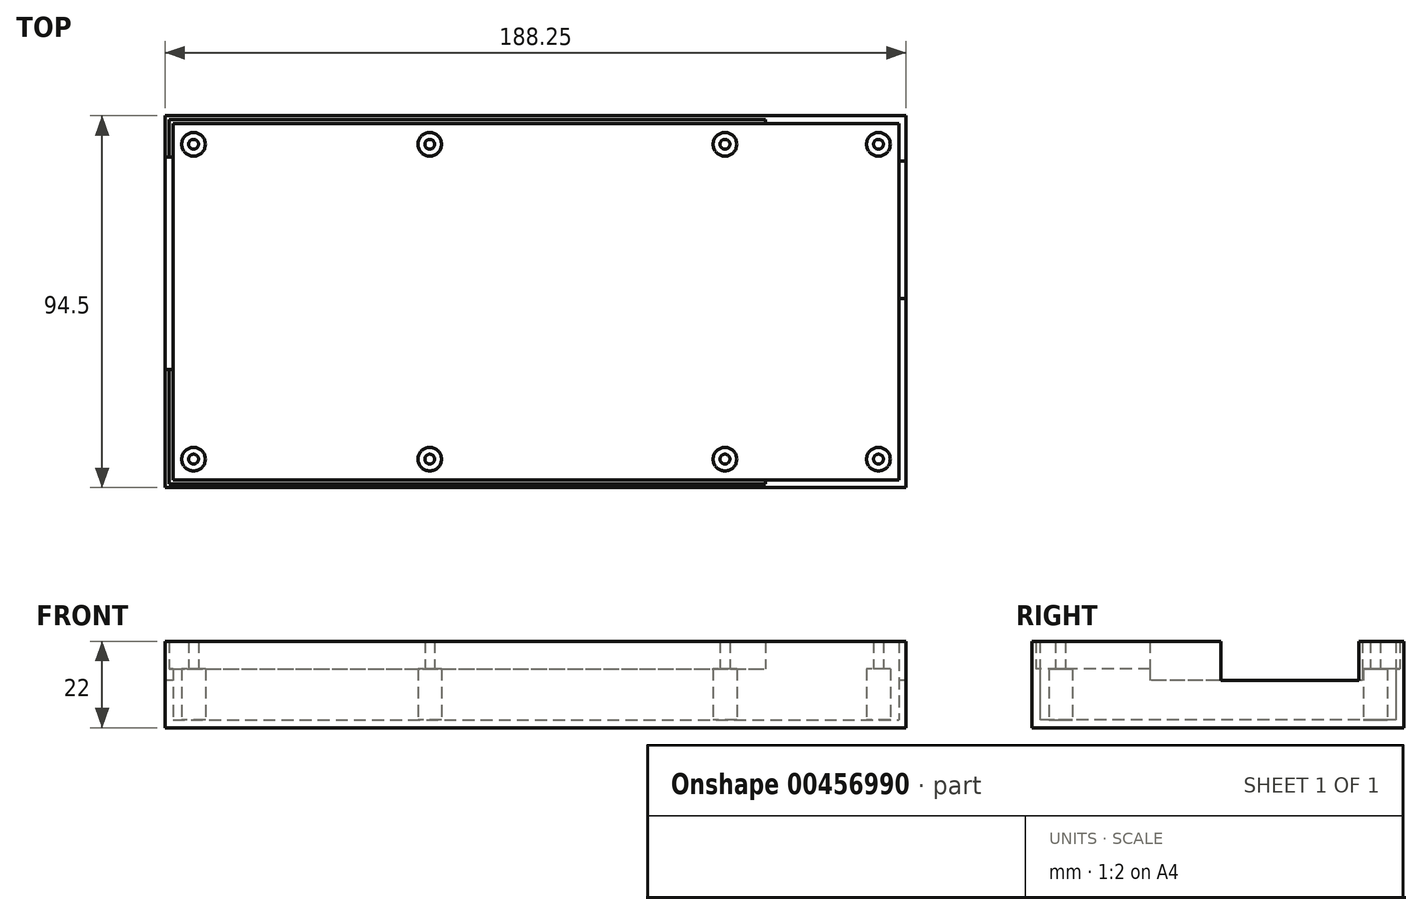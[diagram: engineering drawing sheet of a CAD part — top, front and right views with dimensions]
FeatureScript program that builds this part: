
annotation { "Feature Type Name" : "Feature", "Feature Type Description" : "" }
export const myFeature = defineFeature(function(context is Context, id is Id, definition is map)
    precondition{}
    {
        {
            var Q0;
            Q0=qCreatedBy(makeId("Top.planeOp"),FACE);
            var sketch = newSketch(context, id + "F0", { "sketchPlane" : qUnion([Q0])});
            skLineSegment(sketch, "E0.bottom", {"start": v(-142.25, 0) * mm, "end": v(46, 0) * mm});
            skLineSegment(sketch, "E0.top", {"start": v(-142.25, -94.5) * mm, "end": v(46, -94.5) * mm});
            skLineSegment(sketch, "E0.left", {"start": v(-142.25, 0) * mm, "end": v(-142.25, -94.5) * mm});
            skLineSegment(sketch, "E0.right", {"start": v(46, 0) * mm, "end": v(46, -94.5) * mm});
            skLineSegment(sketch, "E1.bottom", {"start": v(-140.25, -2) * mm, "end": v(44.25, -2) * mm});
            skLineSegment(sketch, "E1.top", {"start": v(-140.25, -92.5) * mm, "end": v(44.25, -92.5) * mm});
            skLineSegment(sketch, "E1.left", {"start": v(-140.25, -2) * mm, "end": v(-140.25, -92.5) * mm});
            skLineSegment(sketch, "E1.right", {"start": v(44.25, -2) * mm, "end": v(44.25, -92.5) * mm});
            skCircle(sketch, "E2", {"center": v(-135, -87.25) * mm, "radius": 3 * mm});
            skCircle(sketch, "E3", {"center": v(-135, -7.25) * mm, "radius": 3 * mm});
            skCircle(sketch, "E4", {"center": v(-75, -87.25) * mm, "radius": 3 * mm});
            skCircle(sketch, "E5", {"center": v(-75, -7.25) * mm, "radius": 3 * mm});
            skCircle(sketch, "E6", {"center": v(0, -7.25) * mm, "radius": 3 * mm});
            skCircle(sketch, "E7", {"center": v(0, -87.25) * mm, "radius": 3 * mm});
            skCircle(sketch, "E8", {"center": v(39, -87.25) * mm, "radius": 3 * mm});
            skCircle(sketch, "E9", {"center": v(39, -7.25) * mm, "radius": 3 * mm});
            skCircle(sketch, "E10", {"center": v(-135, -87.25) * mm, "radius": 1.25 * mm});
            skCircle(sketch, "E11", {"center": v(-75, -87.25) * mm, "radius": 1.25 * mm});
            skCircle(sketch, "E12", {"center": v(0, -87.25) * mm, "radius": 1.25 * mm});
            skCircle(sketch, "E13", {"center": v(39, -87.25) * mm, "radius": 1.25 * mm});
            skCircle(sketch, "E14", {"center": v(-135, -7.25) * mm, "radius": 1.25 * mm});
            skCircle(sketch, "E15", {"center": v(-75, -7.25) * mm, "radius": 1.25 * mm});
            skCircle(sketch, "E16", {"center": v(0, -7.25) * mm, "radius": 1.25 * mm});
            skCircle(sketch, "E17", {"center": v(39, -7.25) * mm, "radius": 1.25 * mm});
            skLineSegment(sketch, "E18", {"start": v(10.25, -2) * mm, "end": v(10.25, 0) * mm});
            skLineSegment(sketch, "E19", {"start": v(10.25, -92.5) * mm, "end": v(10.25, -94.5) * mm});
            skLineSegment(sketch, "E20", {"start": v(10.25, -93.5) * mm, "end": v(-141.25, -93.5) * mm});
            skLineSegment(sketch, "E21", {"start": v(-141.25, -1) * mm, "end": v(-141.25, -93.5) * mm});
            skLineSegment(sketch, "E22", {"start": v(-141.25, -1) * mm, "end": v(10.25, -1) * mm});
            skLineSegment(sketch, "E23", {"start": v(-140.25, -64.5) * mm, "end": v(-141.25, -64.5) * mm});
            skLineSegment(sketch, "E24", {"start": v(-140.25, -10.5) * mm, "end": v(-141.25, -10.5) * mm});
            skLineSegment(sketch, "E25", {"start": v(44.25, -46.5) * mm, "end": v(46, -46.5) * mm});
            skLineSegment(sketch, "E26", {"start": v(46, -11.5) * mm, "end": v(44.25, -11.5) * mm});
            skLineSegment(sketch, "E27", {"start": v(-141.25, -10.5) * mm, "end": v(-142.25, -10.5) * mm});
            skLineSegment(sketch, "E28", {"start": v(-141.25, -64.5) * mm, "end": v(-142.25, -64.5) * mm});
            skSolve(sketch);
        }
        {
            var Q0;
            Q0=makeQuery(id+"F0.imprint","IMPRINT",FACE,{"disambiguationData":[TD([[makeQuery(id+"F0.imprint","IMPRINT",EDGE,{"derivedFrom":sQuery(id+"F0.wireOp",EDGE,"E2")}),-1.0]])]});
            var Q1;
            {var subQ0=sQuery(id+"F0.wireOp",EDGE,"E22");Q1=makeQuery(id+"F0.imprint","IMPRINT",FACE,{"disambiguationData":[TD([[makeQuery(id+"F0.imprint","IMPRINT",EDGE,{"derivedFrom":subQ0}),1.0]])]});}
            var Q2;
            Q2=makeQuery(id+"F0.imprint","IMPRINT",FACE,{"disambiguationData":[TD([[makeQuery(id+"F0.imprint","IMPRINT",EDGE,{"derivedFrom":sQuery(id+"F0.wireOp",EDGE,"E14")}),1.0]])]});
            var Q3;
            Q3=makeQuery(id+"F0.imprint","IMPRINT",FACE,{"disambiguationData":[TD([[makeQuery(id+"F0.imprint","IMPRINT",EDGE,{"derivedFrom":sQuery(id+"F0.wireOp",EDGE,"E3")}),1.0]])]});
            var Q4;
            Q4=makeQuery(id+"F0.imprint","IMPRINT",FACE,{"disambiguationData":[TD([[makeQuery(id+"F0.imprint","IMPRINT",EDGE,{"derivedFrom":sQuery(id+"F0.wireOp",EDGE,"E5")}),1.0]])]});
            var Q5;
            Q5=makeQuery(id+"F0.imprint","IMPRINT",FACE,{"disambiguationData":[TD([[makeQuery(id+"F0.imprint","IMPRINT",EDGE,{"derivedFrom":sQuery(id+"F0.wireOp",EDGE,"E16")}),1.0]])]});
            var Q6;
            Q6=makeQuery(id+"F0.imprint","IMPRINT",FACE,{"disambiguationData":[TD([[makeQuery(id+"F0.imprint","IMPRINT",EDGE,{"derivedFrom":sQuery(id+"F0.wireOp",EDGE,"E17")}),1.0]])]});
            var Q7;
            Q7=makeQuery(id+"F0.imprint","IMPRINT",FACE,{"disambiguationData":[TD([[makeQuery(id+"F0.imprint","IMPRINT",EDGE,{"derivedFrom":sQuery(id+"F0.wireOp",EDGE,"E9")}),1.0]])]});
            var Q8;
            Q8=makeQuery(id+"F0.imprint","IMPRINT",FACE,{"disambiguationData":[TD([[makeQuery(id+"F0.imprint","IMPRINT",EDGE,{"derivedFrom":sQuery(id+"F0.wireOp",EDGE,"E7")}),1.0]])]});
            var Q9;
            Q9=makeQuery(id+"F0.imprint","IMPRINT",FACE,{"disambiguationData":[TD([[makeQuery(id+"F0.imprint","IMPRINT",EDGE,{"derivedFrom":sQuery(id+"F0.wireOp",EDGE,"E6")}),1.0]])]});
            var Q10;
            Q10=makeQuery(id+"F0.imprint","IMPRINT",FACE,{"disambiguationData":[TD([[makeQuery(id+"F0.imprint","IMPRINT",EDGE,{"derivedFrom":sQuery(id+"F0.wireOp",EDGE,"E8")}),1.0]])]});
            var Q11;
            Q11=makeQuery(id+"F0.imprint","IMPRINT",FACE,{"disambiguationData":[TD([[makeQuery(id+"F0.imprint","IMPRINT",EDGE,{"derivedFrom":sQuery(id+"F0.wireOp",EDGE,"E13")}),1.0]])]});
            var Q12;
            Q12=makeQuery(id+"F0.imprint","IMPRINT",FACE,{"disambiguationData":[TD([[makeQuery(id+"F0.imprint","IMPRINT",EDGE,{"derivedFrom":sQuery(id+"F0.wireOp",EDGE,"E12")}),1.0]])]});
            var Q13;
            Q13=makeQuery(id+"F0.imprint","IMPRINT",FACE,{"disambiguationData":[TD([[makeQuery(id+"F0.imprint","IMPRINT",EDGE,{"derivedFrom":sQuery(id+"F0.wireOp",EDGE,"E15")}),1.0]])]});
            var Q14;
            Q14=makeQuery(id+"F0.imprint","IMPRINT",FACE,{"disambiguationData":[TD([[makeQuery(id+"F0.imprint","IMPRINT",EDGE,{"derivedFrom":sQuery(id+"F0.wireOp",EDGE,"E2")}),1.0]])]});
            var Q15;
            Q15=makeQuery(id+"F0.imprint","IMPRINT",FACE,{"disambiguationData":[TD([[makeQuery(id+"F0.imprint","IMPRINT",EDGE,{"derivedFrom":sQuery(id+"F0.wireOp",EDGE,"E10")}),1.0]])]});
            var Q16;
            Q16=makeQuery(id+"F0.imprint","IMPRINT",FACE,{"disambiguationData":[TD([[makeQuery(id+"F0.imprint","IMPRINT",EDGE,{"derivedFrom":sQuery(id+"F0.wireOp",EDGE,"E11")}),1.0]])]});
            var Q17;
            Q17=makeQuery(id+"F0.imprint","IMPRINT",FACE,{"disambiguationData":[TD([[makeQuery(id+"F0.imprint","IMPRINT",EDGE,{"derivedFrom":sQuery(id+"F0.wireOp",EDGE,"E4")}),1.0]])]});
            var Q18;
            {var subQ0=sQuery(id+"F0.wireOp",EDGE,"E25");Q18=makeQuery(id+"F0.imprint","IMPRINT",FACE,{"disambiguationData":[TD([[makeQuery(id+"F0.imprint","IMPRINT",EDGE,{"derivedFrom":subQ0}),1.0]])]});}
            var Q19;
            {var subQ0=sQuery(id+"F0.wireOp",EDGE,"E23");var subQ1=sQuery(id+"F0.wireOp",EDGE,"E1.left");var subQ2=makeQuery(id+"F0.imprint","INTERSECT",VERTEX,{"derivedFrom":[subQ1,subQ0]});Q19=makeQuery(id+"F0.imprint","IMPRINT",FACE,{"disambiguationData":[TD([[makeQuery(id+"F0.imprint","IMPRINT",EDGE,{"disambiguationData":[TD([[subQ2,1.0]])],"derivedFrom":subQ1}),-1.0]])]});}
            var Q20;
            {var subQ0=sQuery(id+"F0.wireOp",EDGE,"E22");Q20=makeQuery(id+"F0.imprint","IMPRINT",FACE,{"disambiguationData":[TD([[makeQuery(id+"F0.imprint","IMPRINT",EDGE,{"derivedFrom":subQ0}),-1.0]])]});}
            var Q21;
            {var subQ3=sQuery(id+"F0.wireOp",EDGE,"E26");Q21=makeQuery(id+"F0.imprint","IMPRINT",FACE,{"disambiguationData":[TD([[makeQuery(id+"F0.imprint","IMPRINT",EDGE,{"derivedFrom":subQ3}),-1.0]])]});}
            var Q22;
            {var subQ0=sQuery(id+"F0.wireOp",EDGE,"E20");Q22=makeQuery(id+"F0.imprint","IMPRINT",FACE,{"disambiguationData":[TD([[makeQuery(id+"F0.imprint","IMPRINT",EDGE,{"derivedFrom":subQ0}),-1.0]])]});}
            var Q23;
            {var subQ3=sQuery(id+"F0.wireOp",EDGE,"E25");Q23=makeQuery(id+"F0.imprint","IMPRINT",FACE,{"disambiguationData":[TD([[makeQuery(id+"F0.imprint","IMPRINT",EDGE,{"derivedFrom":subQ3}),-1.0]])]});}
            var Q24;
            {var subQ0=sQuery(id+"F0.wireOp",EDGE,"E20");Q24=makeQuery(id+"F0.imprint","IMPRINT",FACE,{"disambiguationData":[TD([[makeQuery(id+"F0.imprint","IMPRINT",EDGE,{"derivedFrom":subQ0}),1.0]])]});}
            var Q25;
            {var subQ0=sQuery(id+"F0.wireOp",EDGE,"E23");var subQ1=sQuery(id+"F0.wireOp",EDGE,"E0.left");var subQ2=makeQuery(id+"F0.imprint","INTERSECT",VERTEX,{"derivedFrom":[subQ1,subQ0]});Q25=makeQuery(id+"F0.imprint","IMPRINT",FACE,{"disambiguationData":[TD([[makeQuery(id+"F0.imprint","IMPRINT",EDGE,{"disambiguationData":[TD([[subQ2,1.0]])],"derivedFrom":subQ1}),1.0]])]});}
            extrude(context, id + "F1", {"entities" : qUnion([Q0, Q1, Q2, Q3, Q4, Q5, Q6, Q7, Q8, Q9, Q10, Q11, Q12, Q13, Q14, Q15, Q16, Q17, Q18, Q19, Q20, Q21, Q22, Q23, Q24, Q25]), "oppositeDirection" : true, "depth" : 2 * mm, "offsetDistance" : 25 * mm});
        }
        {
            var Q0;
            Q0=makeQuery(id+"F0.imprint","IMPRINT",FACE,{"disambiguationData":[TD([[makeQuery(id+"F0.imprint","IMPRINT",EDGE,{"derivedFrom":sQuery(id+"F0.wireOp",EDGE,"E0.bottom")}),-1.0]])]});
            var Q1;
            {var subQ3=sQuery(id+"F0.wireOp",EDGE,"E26");Q1=makeQuery(id+"F0.imprint","IMPRINT",FACE,{"disambiguationData":[TD([[makeQuery(id+"F0.imprint","IMPRINT",EDGE,{"derivedFrom":subQ3}),-1.0]])]});}
            var Q2;
            {var subQ3=sQuery(id+"F0.wireOp",EDGE,"E25");Q2=makeQuery(id+"F0.imprint","IMPRINT",FACE,{"disambiguationData":[TD([[makeQuery(id+"F0.imprint","IMPRINT",EDGE,{"derivedFrom":subQ3}),-1.0]])]});}
            var Q3;
            {var subQ0=sQuery(id+"F0.wireOp",EDGE,"E20");Q3=makeQuery(id+"F0.imprint","IMPRINT",FACE,{"disambiguationData":[TD([[makeQuery(id+"F0.imprint","IMPRINT",EDGE,{"derivedFrom":subQ0}),1.0]])]});}
            extrude(context, id + "F2", {"entities" : qUnion([Q0, Q1, Q2, Q3]), "operationType" : NewBodyOperationType.ADD, "depth" : 20 * mm, "offsetDistance" : 25 * mm});
        }
        {
            var Q0;
            {var subQ0=sQuery(id+"F0.wireOp",EDGE,"E22");Q0=makeQuery(id+"F0.imprint","IMPRINT",FACE,{"disambiguationData":[TD([[makeQuery(id+"F0.imprint","IMPRINT",EDGE,{"derivedFrom":subQ0}),-1.0]])]});}
            var Q1;
            {var subQ0=sQuery(id+"F0.wireOp",EDGE,"E20");Q1=makeQuery(id+"F0.imprint","IMPRINT",FACE,{"disambiguationData":[TD([[makeQuery(id+"F0.imprint","IMPRINT",EDGE,{"derivedFrom":subQ0}),-1.0]])]});}
            extrude(context, id + "F3", {"entities" : qUnion([Q0, Q1]), "operationType" : NewBodyOperationType.ADD, "depth" : 13 * mm, "offsetDistance" : 25 * mm});
        }
        {
            var Q0;
            {var subQ0=sQuery(id+"F0.wireOp",EDGE,"E23");Q0=makeQuery(id+"F0.imprint","IMPRINT",FACE,{"disambiguationData":[TD([[makeQuery(id+"F0.imprint","IMPRINT",EDGE,{"derivedFrom":subQ0}),-1.0]])]});}
            var Q1;
            {var subQ0=sQuery(id+"F0.wireOp",EDGE,"E27");Q1=makeQuery(id+"F0.imprint","IMPRINT",FACE,{"disambiguationData":[TD([[makeQuery(id+"F0.imprint","IMPRINT",EDGE,{"derivedFrom":subQ0}),1.0]])]});}
            var Q2;
            {var subQ0=sQuery(id+"F0.wireOp",EDGE,"E25");Q2=makeQuery(id+"F0.imprint","IMPRINT",FACE,{"disambiguationData":[TD([[makeQuery(id+"F0.imprint","IMPRINT",EDGE,{"derivedFrom":subQ0}),1.0]])]});}
            extrude(context, id + "F4", {"entities" : qUnion([Q0, Q1, Q2]), "operationType" : NewBodyOperationType.ADD, "depth" : 10 * mm, "offsetDistance" : 25 * mm});
        }
        {
            var Q0;
            Q0=makeQuery(id+"F0.imprint","IMPRINT",FACE,{"disambiguationData":[TD([[makeQuery(id+"F0.imprint","IMPRINT",EDGE,{"derivedFrom":sQuery(id+"F0.wireOp",EDGE,"E14")}),1.0]])]});
            var Q1;
            Q1=makeQuery(id+"F0.imprint","IMPRINT",FACE,{"disambiguationData":[TD([[makeQuery(id+"F0.imprint","IMPRINT",EDGE,{"derivedFrom":sQuery(id+"F0.wireOp",EDGE,"E15")}),1.0]])]});
            var Q2;
            Q2=makeQuery(id+"F0.imprint","IMPRINT",FACE,{"disambiguationData":[TD([[makeQuery(id+"F0.imprint","IMPRINT",EDGE,{"derivedFrom":sQuery(id+"F0.wireOp",EDGE,"E16")}),1.0]])]});
            var Q3;
            Q3=makeQuery(id+"F0.imprint","IMPRINT",FACE,{"disambiguationData":[TD([[makeQuery(id+"F0.imprint","IMPRINT",EDGE,{"derivedFrom":sQuery(id+"F0.wireOp",EDGE,"E17")}),1.0]])]});
            var Q4;
            Q4=makeQuery(id+"F0.imprint","IMPRINT",FACE,{"disambiguationData":[TD([[makeQuery(id+"F0.imprint","IMPRINT",EDGE,{"derivedFrom":sQuery(id+"F0.wireOp",EDGE,"E13")}),1.0]])]});
            var Q5;
            Q5=makeQuery(id+"F0.imprint","IMPRINT",FACE,{"disambiguationData":[TD([[makeQuery(id+"F0.imprint","IMPRINT",EDGE,{"derivedFrom":sQuery(id+"F0.wireOp",EDGE,"E12")}),1.0]])]});
            var Q6;
            Q6=makeQuery(id+"F0.imprint","IMPRINT",FACE,{"disambiguationData":[TD([[makeQuery(id+"F0.imprint","IMPRINT",EDGE,{"derivedFrom":sQuery(id+"F0.wireOp",EDGE,"E11")}),1.0]])]});
            var Q7;
            Q7=makeQuery(id+"F0.imprint","IMPRINT",FACE,{"disambiguationData":[TD([[makeQuery(id+"F0.imprint","IMPRINT",EDGE,{"derivedFrom":sQuery(id+"F0.wireOp",EDGE,"E10")}),1.0]])]});
            extrude(context, id + "F5", {"entities" : qUnion([Q0, Q1, Q2, Q3, Q4, Q5, Q6, Q7]), "operationType" : NewBodyOperationType.ADD, "depth" : 20 * mm, "offsetDistance" : 25 * mm});
        }
        {
            var Q0;
            Q0=makeQuery(id+"F0.imprint","IMPRINT",FACE,{"disambiguationData":[TD([[makeQuery(id+"F0.imprint","IMPRINT",EDGE,{"derivedFrom":sQuery(id+"F0.wireOp",EDGE,"E3")}),1.0]])]});
            var Q1;
            Q1=makeQuery(id+"F0.imprint","IMPRINT",FACE,{"disambiguationData":[TD([[makeQuery(id+"F0.imprint","IMPRINT",EDGE,{"derivedFrom":sQuery(id+"F0.wireOp",EDGE,"E5")}),1.0]])]});
            var Q2;
            Q2=makeQuery(id+"F0.imprint","IMPRINT",FACE,{"disambiguationData":[TD([[makeQuery(id+"F0.imprint","IMPRINT",EDGE,{"derivedFrom":sQuery(id+"F0.wireOp",EDGE,"E6")}),1.0]])]});
            var Q3;
            Q3=makeQuery(id+"F0.imprint","IMPRINT",FACE,{"disambiguationData":[TD([[makeQuery(id+"F0.imprint","IMPRINT",EDGE,{"derivedFrom":sQuery(id+"F0.wireOp",EDGE,"E9")}),1.0]])]});
            var Q4;
            Q4=makeQuery(id+"F0.imprint","IMPRINT",FACE,{"disambiguationData":[TD([[makeQuery(id+"F0.imprint","IMPRINT",EDGE,{"derivedFrom":sQuery(id+"F0.wireOp",EDGE,"E2")}),1.0]])]});
            var Q5;
            Q5=makeQuery(id+"F0.imprint","IMPRINT",FACE,{"disambiguationData":[TD([[makeQuery(id+"F0.imprint","IMPRINT",EDGE,{"derivedFrom":sQuery(id+"F0.wireOp",EDGE,"E4")}),1.0]])]});
            var Q6;
            Q6=makeQuery(id+"F0.imprint","IMPRINT",FACE,{"disambiguationData":[TD([[makeQuery(id+"F0.imprint","IMPRINT",EDGE,{"derivedFrom":sQuery(id+"F0.wireOp",EDGE,"E7")}),1.0]])]});
            var Q7;
            Q7=makeQuery(id+"F0.imprint","IMPRINT",FACE,{"disambiguationData":[TD([[makeQuery(id+"F0.imprint","IMPRINT",EDGE,{"derivedFrom":sQuery(id+"F0.wireOp",EDGE,"E8")}),1.0]])]});
            extrude(context, id + "F6", {"entities" : qUnion([Q0, Q1, Q2, Q3, Q4, Q5, Q6, Q7]), "operationType" : NewBodyOperationType.ADD, "depth" : 13 * mm, "offsetDistance" : 25 * mm});
        }
    });
